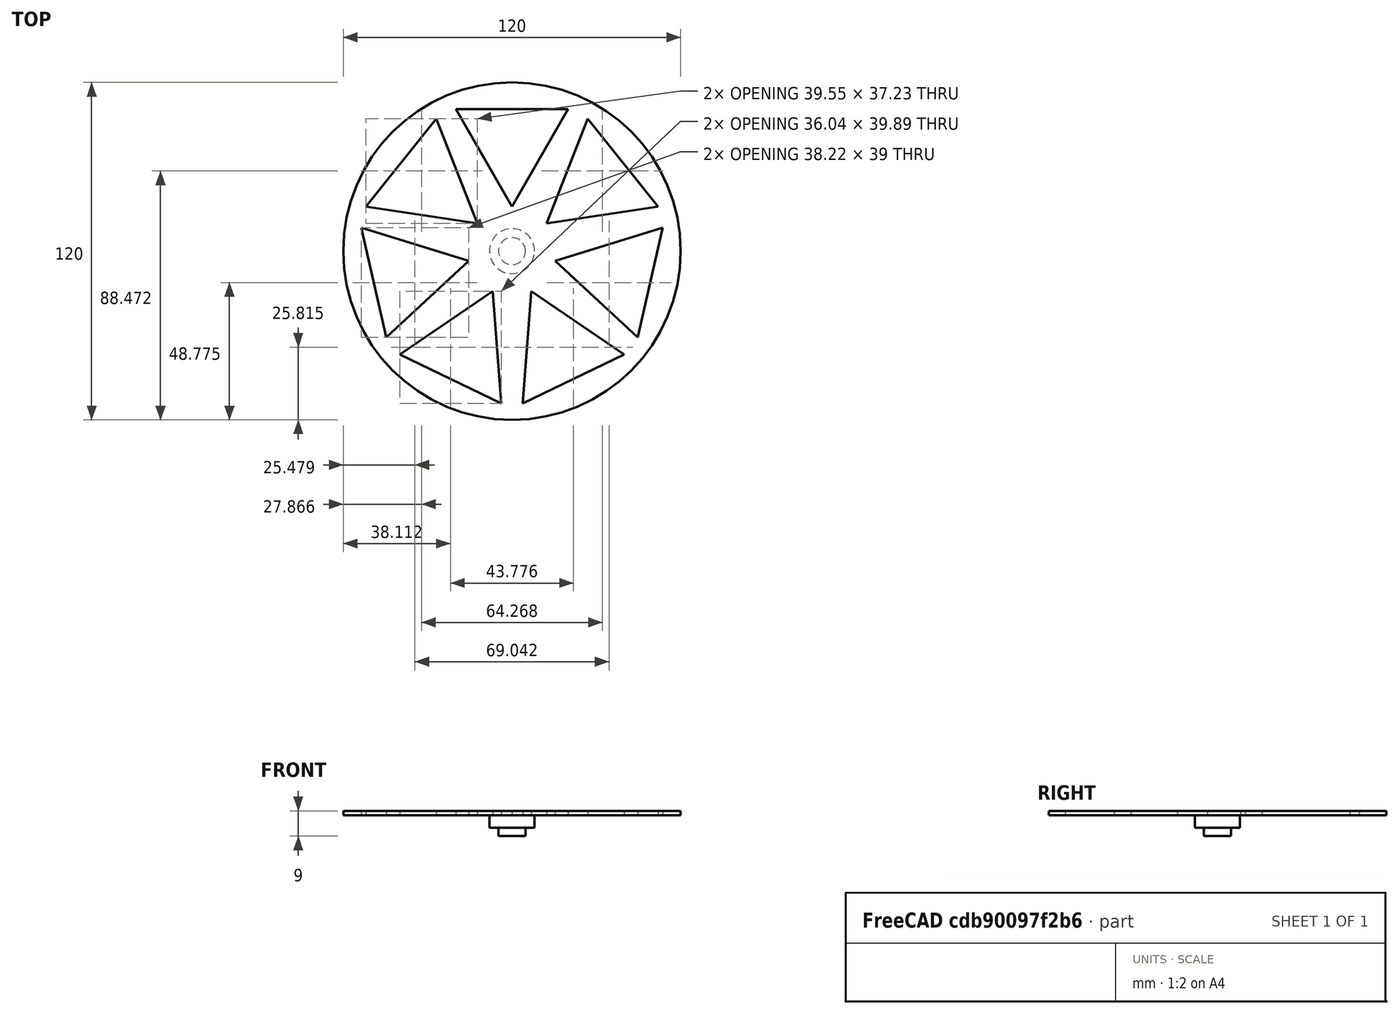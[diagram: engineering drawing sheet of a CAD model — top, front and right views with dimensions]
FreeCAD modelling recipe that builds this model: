
FCSTD DOCUMENT  (FreeCAD 0.16R)
Label: FakeDisc120mm
License: All rights reserved
LicenseURL: http://en.wikipedia.org/wiki/All_rights_reserved
objects: Sketcher::SketchObject×4, PartDesign::Pad×3, PartDesign::Pocket×1, PartDesign::PolarPattern×1, Mesh::Feature×1
note: 13 computed .brp shape members not serialized (recipe doc carries the construction recipe); baked Part::Feature solids carry a one-line shape summary decoded from their .brp

FEATURE [Sketcher::SketchObject] Sketch
  sketch-geometry (1):
    g0: Circle CenterX=0 CenterY=0 CenterZ=0 NormalX=0 NormalY=0 NormalZ=1 Radius=60
  constraints (2):
    c: Radius(g0) = 60
    c: Coincident(g0,g-1)
FEATURE [PartDesign::Pad] Pad
  Length = 1.6
  Length2 = 100
  Sketch = -> Sketch
  Type = 0
FEATURE [Sketcher::SketchObject] Sketch001
  Placement = pos=(0,0,1.6) rot=(0,0,1;0rad)
  Support = -> Pad [Face3]
  sketch-geometry (1):
    g0: Circle CenterX=0 CenterY=0 CenterZ=0 NormalX=0 NormalY=0 NormalZ=1 Radius=8
  constraints (2):
    c: Radius(g0) = 8
    c: Coincident(g0,g-1)
FEATURE [PartDesign::Pad] Pad001
  Length = 6
  Length2 = 100
  Reversed = true
  Sketch = -> Sketch001
  Type = 0
FEATURE [Sketcher::SketchObject] Sketch002
  Placement = pos=(0,0,1.6) rot=(0,0,1;0rad)
  Support = -> Pad001 [Face5]
  sketch-geometry (1):
    g0: Circle CenterX=0 CenterY=0 CenterZ=0 NormalX=0 NormalY=0 NormalZ=1 Radius=4.8
  constraints (2):
    c: Radius(g0) = 4.8
    c: Coincident(g0,g-1)
FEATURE [PartDesign::Pad] Pad002
  Length = 9
  Length2 = 100
  Reversed = true
  Sketch = -> Sketch002
  Type = 0
FEATURE [Sketcher::SketchObject] Sketch003
  Placement = pos=(0,0,1.6) rot=(0,0,1;0rad)
  Support = -> Pad002 [Face3]
  sketch-geometry (3):
    g0: LineSegment StartX=-20 StartY=50.4467 StartZ=0 EndX=20 EndY=50.4467 EndZ=0
    g1: LineSegment StartX=20 StartY=50.4467 StartZ=0 EndX=0 EndY=15.8057 EndZ=0
    g2: LineSegment StartX=0 StartY=15.8057 StartZ=0 EndX=-20 EndY=50.4467 EndZ=0
  constraints (8):
    c: Coincident(g0,g1)
    c: PointOnObject(g1,g-2)
    c: Coincident(g1,g2)
    c: Coincident(g2,g0)
    c: Symmetric(g0,g0,g-2)
    c: Distance(g1) = 40
    c: Equal(g2,g1)
    c: Distance(g0) = 40
FEATURE [PartDesign::Pocket] Pocket
  Length = 5
  Sketch = -> Sketch003
  Type = 1
FEATURE [PartDesign::PolarPattern] PolarPattern
  Angle = 360
  Axis = -> Sketch003 [N_Axis]
  Occurrences = 7
  Originals = -> [Pocket]
FEATURE [Mesh::Feature] Mesh  label="PolarPattern (Meshed)"
